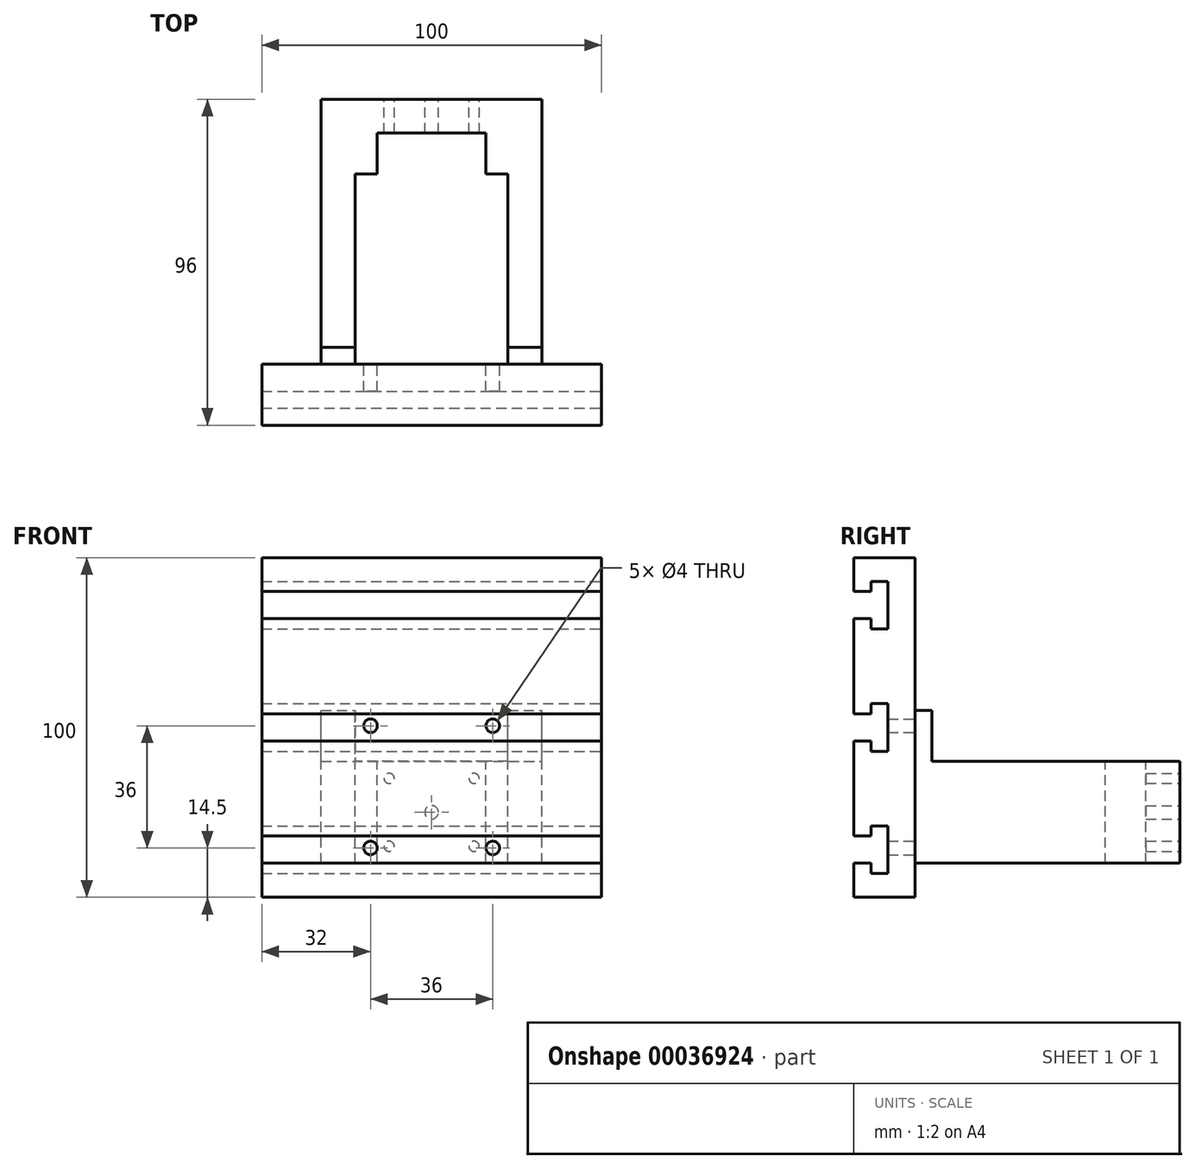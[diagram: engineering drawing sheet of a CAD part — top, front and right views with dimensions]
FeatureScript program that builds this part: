
annotation { "Feature Type Name" : "Feature", "Feature Type Description" : "" }
export const myFeature = defineFeature(function(context is Context, id is Id, definition is map)
    precondition{}
    {
        {
            var Q0;
            Q0=qCreatedBy(makeId("Front.planeOp"),FACE);
            var sketch = newSketch(context, id + "F0", { "sketchPlane" : qUnion([Q0])});
            skLineSegment(sketch, "E0.bottom", {"start": v(-50, 100) * mm, "end": v(50, 100) * mm});
            skLineSegment(sketch, "E0.top", {"start": v(-50, 0) * mm, "end": v(50, 0) * mm});
            skLineSegment(sketch, "E0.left", {"start": v(-50, 100) * mm, "end": v(-50, 0) * mm});
            skLineSegment(sketch, "E0.right", {"start": v(50, 100) * mm, "end": v(50, 0) * mm});
            skSolve(sketch);
        }
        {
            var Q0;
            Q0 = qSketchRegion(id + "F0", true);
            extrude(context, id + "F1", {"entities" : qUnion([Q0]), "oppositeDirection" : true, "depth" : 96 * mm});
        }
        {
            var Q0;
            Q0=makeQuery(id+"F1.opExtrude","SWEPT_FACE",FACE,{"disambiguationData":[OSD([sQuery(id+"F0.wireOp",EDGE,"E0.bottom")])]});
            var sketch = newSketch(context, id + "F2", { "sketchPlane" : qUnion([Q0])});
            skLineSegment(sketch, "E1.bottom", {"start": v(-50, 96) * mm, "end": v(-32.5, 96) * mm});
            skLineSegment(sketch, "E1.top", {"start": v(-50, 18) * mm, "end": v(-32.5, 18) * mm});
            skLineSegment(sketch, "E1.left", {"start": v(-50, 96) * mm, "end": v(-50, 18) * mm});
            skLineSegment(sketch, "E1.right", {"start": v(-32.5, 96) * mm, "end": v(-32.5, 18) * mm});
            skLineSegment(sketch, "E2.MirrorCS", {"start": v(50, 96) * mm, "end": v(32.5, 96) * mm});
            skLineSegment(sketch, "E3.MirrorCS", {"start": v(50, 96) * mm, "end": v(50, 18) * mm});
            skLineSegment(sketch, "E4.MirrorCS", {"start": v(32.5, 96) * mm, "end": v(32.5, 18) * mm});
            skLineSegment(sketch, "E5.MirrorCS", {"start": v(50, 18) * mm, "end": v(32.5, 18) * mm});
            skLineSegment(sketch, "E6", {"start": v(-22.5, 18) * mm, "end": v(-22.5, 74) * mm});
            skLineSegment(sketch, "E7", {"start": v(-22.5, 74) * mm, "end": v(-16, 74) * mm});
            skLineSegment(sketch, "E8", {"start": v(-16, 74) * mm, "end": v(-16, 86) * mm});
            skLineSegment(sketch, "E9", {"start": v(-16, 86) * mm, "end": v(16, 86) * mm});
            skLineSegment(sketch, "E10", {"start": v(16, 86) * mm, "end": v(16, 74) * mm});
            skLineSegment(sketch, "E11", {"start": v(16, 74) * mm, "end": v(22.5, 74) * mm});
            skLineSegment(sketch, "E12", {"start": v(22.5, 74) * mm, "end": v(22.5, 18) * mm});
            skLineSegment(sketch, "E13", {"start": v(22.5, 18) * mm, "end": v(-22.5, 18) * mm});
            skSolve(sketch);
        }
        {
            var Q0;
            Q0 = qSketchRegion(id + "F2", true);
            extrude(context, id + "F3", {"entities" : qUnion([Q0]), "operationType" : NewBodyOperationType.REMOVE, "endBound" : BoundingType.THROUGH_ALL, "oppositeDirection" : true, "depth" : 25 * mm});
        }
        {
            var Q0;
            Q0=makeQuery(id+"F1.opExtrude","SWEPT_FACE",FACE,{"disambiguationData":[OSD([sQuery(id+"F0.wireOp",EDGE,"E0.bottom")])]});
            var sketch = newSketch(context, id + "F4", { "sketchPlane" : qUnion([Q0])});
            skLineSegment(sketch, "E14.bottom", {"start": v(-32.5, 96) * mm, "end": v(32.5, 96) * mm});
            skLineSegment(sketch, "E14.top", {"start": v(-32.5, 18) * mm, "end": v(32.5, 18) * mm});
            skLineSegment(sketch, "E14.left", {"start": v(-32.5, 96) * mm, "end": v(-32.5, 18) * mm});
            skLineSegment(sketch, "E14.right", {"start": v(32.5, 96) * mm, "end": v(32.5, 18) * mm});
            skSolve(sketch);
        }
        {
            var Q0;
            Q0 = qSketchRegion(id + "F4", true);
            extrude(context, id + "F5", {"entities" : qUnion([Q0]), "operationType" : NewBodyOperationType.REMOVE, "oppositeDirection" : true, "depth" : 45 * mm});
        }
        {
            var Q0;
            Q0=makeQuery(id+"F1.opExtrude","SWEPT_FACE",FACE,{"disambiguationData":[OSD([sQuery(id+"F0.wireOp",EDGE,"E0.top")])]});
            var sketch = newSketch(context, id + "F6", { "sketchPlane" : qUnion([Q0])});
            skLineSegment(sketch, "E15.bottom", {"start": v(-32.5, -18) * mm, "end": v(32.5, -18) * mm});
            skLineSegment(sketch, "E15.top", {"start": v(-32.5, -96) * mm, "end": v(32.5, -96) * mm});
            skLineSegment(sketch, "E15.left", {"start": v(-32.5, -18) * mm, "end": v(-32.5, -96) * mm});
            skLineSegment(sketch, "E15.right", {"start": v(32.5, -18) * mm, "end": v(32.5, -96) * mm});
            skSolve(sketch);
        }
        {
            var Q0;
            Q0 = qSketchRegion(id + "F6", true);
            extrude(context, id + "F7", {"entities" : qUnion([Q0]), "operationType" : NewBodyOperationType.REMOVE, "oppositeDirection" : true, "depth" : 10 * mm});
        }
        {
            var Q0;
            Q0=makeQuery(id+"F5.boolean.opBoolean","COPY",FACE,{"derivedFrom":makeQuery(id+"F5.opExtrude","CAP_FACE",FACE,{"disambiguationData":[OSD([sQuery(id+"F4.wireOp",EDGE,"E14.bottom"),sQuery(id+"F4.wireOp",EDGE,"E14.top"),sQuery(id+"F4.wireOp",EDGE,"E14.left"),sQuery(id+"F4.wireOp",EDGE,"E14.right")])],"isStart":false})});
            var sketch = newSketch(context, id + "F8", { "sketchPlane" : qUnion([Q0])});
            skLineSegment(sketch, "E16.bottom", {"start": v(-32.5, 96) * mm, "end": v(32.5, 96) * mm});
            skLineSegment(sketch, "E16.top", {"start": v(-32.5, 23) * mm, "end": v(32.5, 23) * mm});
            skLineSegment(sketch, "E16.left", {"start": v(-32.5, 96) * mm, "end": v(-32.5, 23) * mm});
            skLineSegment(sketch, "E16.right", {"start": v(32.5, 96) * mm, "end": v(32.5, 23) * mm});
            skSolve(sketch);
        }
        {
            var Q0;
            Q0 = qSketchRegion(id + "F8", true);
            extrude(context, id + "F9", {"entities" : qUnion([Q0]), "operationType" : NewBodyOperationType.REMOVE, "oppositeDirection" : true, "depth" : 15 * mm});
        }
        {
            var Q0;
            Q0=makeQuery(id+"F1.opExtrude","SWEPT_FACE",FACE,{"disambiguationData":[OSD([sQuery(id+"F0.wireOp",EDGE,"E0.right")])]});
            var sketch = newSketch(context, id + "F10", { "sketchPlane" : qUnion([Q0])});
            skLineSegment(sketch, "E17", {"start": v(0, 10) * mm, "end": v(5, 10) * mm});
            skLineSegment(sketch, "E18", {"start": v(5, 10) * mm, "end": v(5, 7) * mm});
            skLineSegment(sketch, "E19", {"start": v(5, 7) * mm, "end": v(10, 7) * mm});
            skLineSegment(sketch, "E20", {"start": v(10, 7) * mm, "end": v(10, 21) * mm});
            skLineSegment(sketch, "E21", {"start": v(10, 21) * mm, "end": v(5, 21) * mm});
            skLineSegment(sketch, "E22", {"start": v(5, 21) * mm, "end": v(5, 18) * mm});
            skLineSegment(sketch, "E23", {"start": v(5, 18) * mm, "end": v(0, 18) * mm});
            skLineSegment(sketch, "E24", {"start": v(0, 18) * mm, "end": v(0, 10) * mm});
            skLineSegment(sketch, "E25.0.1.0", {"start": v(5, 43) * mm, "end": v(10, 43) * mm});
            skLineSegment(sketch, "E25.0.1.1", {"start": v(5, 57) * mm, "end": v(5, 54) * mm});
            skLineSegment(sketch, "E25.0.1.2", {"start": v(10, 57) * mm, "end": v(5, 57) * mm});
            skLineSegment(sketch, "E25.0.1.3", {"start": v(10, 43) * mm, "end": v(10, 57) * mm});
            skLineSegment(sketch, "E25.0.1.4", {"start": v(0, 46) * mm, "end": v(5, 46) * mm});
            skLineSegment(sketch, "E25.0.1.5", {"start": v(5, 54) * mm, "end": v(0, 54) * mm});
            skLineSegment(sketch, "E25.0.1.6", {"start": v(0, 54) * mm, "end": v(0, 46) * mm});
            skLineSegment(sketch, "E25.0.1.7", {"start": v(5, 46) * mm, "end": v(5, 43) * mm});
            skLineSegment(sketch, "E25.0.2.0", {"start": v(5, 79) * mm, "end": v(10, 79) * mm});
            skLineSegment(sketch, "E25.0.2.1", {"start": v(5, 93) * mm, "end": v(5, 90) * mm});
            skLineSegment(sketch, "E25.0.2.2", {"start": v(10, 93) * mm, "end": v(5, 93) * mm});
            skLineSegment(sketch, "E25.0.2.3", {"start": v(10, 79) * mm, "end": v(10, 93) * mm});
            skLineSegment(sketch, "E25.0.2.4", {"start": v(0, 82) * mm, "end": v(5, 82) * mm});
            skLineSegment(sketch, "E25.0.2.5", {"start": v(5, 90) * mm, "end": v(0, 90) * mm});
            skLineSegment(sketch, "E25.0.2.6", {"start": v(0, 90) * mm, "end": v(0, 82) * mm});
            skLineSegment(sketch, "E25.0.2.7", {"start": v(5, 82) * mm, "end": v(5, 79) * mm});
            skLineSegment(sketch, "E25.direction1", {"start": v(5, 7) * mm, "end": v(30, 7) * mm, "construction": true});
            skLineSegment(sketch, "E25.direction2", {"start": v(5, 7) * mm, "end": v(5, 43) * mm, "construction": true});
            skSolve(sketch);
        }
        {
            var Q0;
            Q0 = qSketchRegion(id + "F10", true);
            extrude(context, id + "F11", {"entities" : qUnion([Q0]), "operationType" : NewBodyOperationType.REMOVE, "endBound" : BoundingType.THROUGH_ALL, "oppositeDirection" : true, "depth" : 25 * mm});
        }
        {
            var Q0;
            Q0=makeQuery(id+"F1.opExtrude","CAP_FACE",FACE,{"disambiguationData":[OSD([sQuery(id+"F0.wireOp",EDGE,"E0.bottom"),sQuery(id+"F0.wireOp",EDGE,"E0.top"),sQuery(id+"F0.wireOp",EDGE,"E0.left"),sQuery(id+"F0.wireOp",EDGE,"E0.right")])],"isStart":false});
            var sketch = newSketch(context, id + "F12", { "sketchPlane" : qUnion([Q0])});
            skPoint(sketch, "E26.rect.middle", {"position": v(0, 25) * mm});
            skCircle(sketch, "E27", {"center": v(-12.5, 35) * mm, "radius": 1.5 * mm});
            skCircle(sketch, "E28.0.1.0", {"center": v(-12.5, 15) * mm, "radius": 1.5 * mm});
            skCircle(sketch, "E28.1.0.0", {"center": v(12.5, 35) * mm, "radius": 1.5 * mm});
            skCircle(sketch, "E28.1.1.0", {"center": v(12.5, 15) * mm, "radius": 1.5 * mm});
            skCircle(sketch, "E29", {"center": v(0, 25) * mm, "radius": 2 * mm});
            skSolve(sketch);
        }
        {
            var Q0;
            Q0 = qSketchRegion(id + "F12", true);
            extrude(context, id + "F13", {"entities" : qUnion([Q0]), "operationType" : NewBodyOperationType.REMOVE, "oppositeDirection" : true, "depth" : 10 * mm});
        }
        {
            var Q0;
            Q0=makeQuery(id+"F7.boolean.opBoolean","MERGE",FACE,{"derivedFrom":[makeQuery(id+"F5.boolean.opBoolean","MERGE",FACE,{"derivedFrom":[makeQuery(id+"F3.boolean.opBoolean","COPY",FACE,{"derivedFrom":makeQuery(id+"F3.opExtrude","SWEPT_FACE",FACE,{"disambiguationData":[OSD([sQuery(id+"F2.wireOp",EDGE,"E1.top")])]})}),makeQuery(id+"F3.boolean.opBoolean","COPY",FACE,{"derivedFrom":makeQuery(id+"F3.opExtrude","SWEPT_FACE",FACE,{"disambiguationData":[OSD([sQuery(id+"F2.wireOp",EDGE,"E5.MirrorCS")])]})}),makeQuery(id+"F3.boolean.opBoolean","COPY",FACE,{"derivedFrom":makeQuery(id+"F3.opExtrude","SWEPT_FACE",FACE,{"disambiguationData":[OSD([sQuery(id+"F2.wireOp",EDGE,"E13")])]})}),makeQuery(id+"F5.opExtrude","SWEPT_FACE",FACE,{"disambiguationData":[OSD([sQuery(id+"F4.wireOp",EDGE,"E14.top")])]})]}),makeQuery(id+"F7.opExtrude","SWEPT_FACE",FACE,{"disambiguationData":[OSD([sQuery(id+"F6.wireOp",EDGE,"E15.bottom")])]})]});
            var sketch = newSketch(context, id + "F14", { "sketchPlane" : qUnion([Q0])});
            skLineSegment(sketch, "E30.top", {"start": v(22.5, 10) * mm, "end": v(-22.5, 10) * mm});
            skPoint(sketch, "E31.rect.middle", {"position": v(0, 32.5) * mm});
            skCircle(sketch, "E32", {"center": v(18, 50.5) * mm, "radius": 2 * mm});
            skCircle(sketch, "E33.0.1.0", {"center": v(18, 14.5) * mm, "radius": 2 * mm});
            skCircle(sketch, "E33.1.0.0", {"center": v(-18, 50.5) * mm, "radius": 2 * mm});
            skCircle(sketch, "E33.1.1.0", {"center": v(-18, 14.5) * mm, "radius": 2 * mm});
            skSolve(sketch);
        }
        {
            var Q0;
            Q0 = qSketchRegion(id + "F14", true);
            extrude(context, id + "F15", {"entities" : qUnion([Q0]), "operationType" : NewBodyOperationType.REMOVE, "oppositeDirection" : true, "depth" : 8 * mm});
        }
    });
